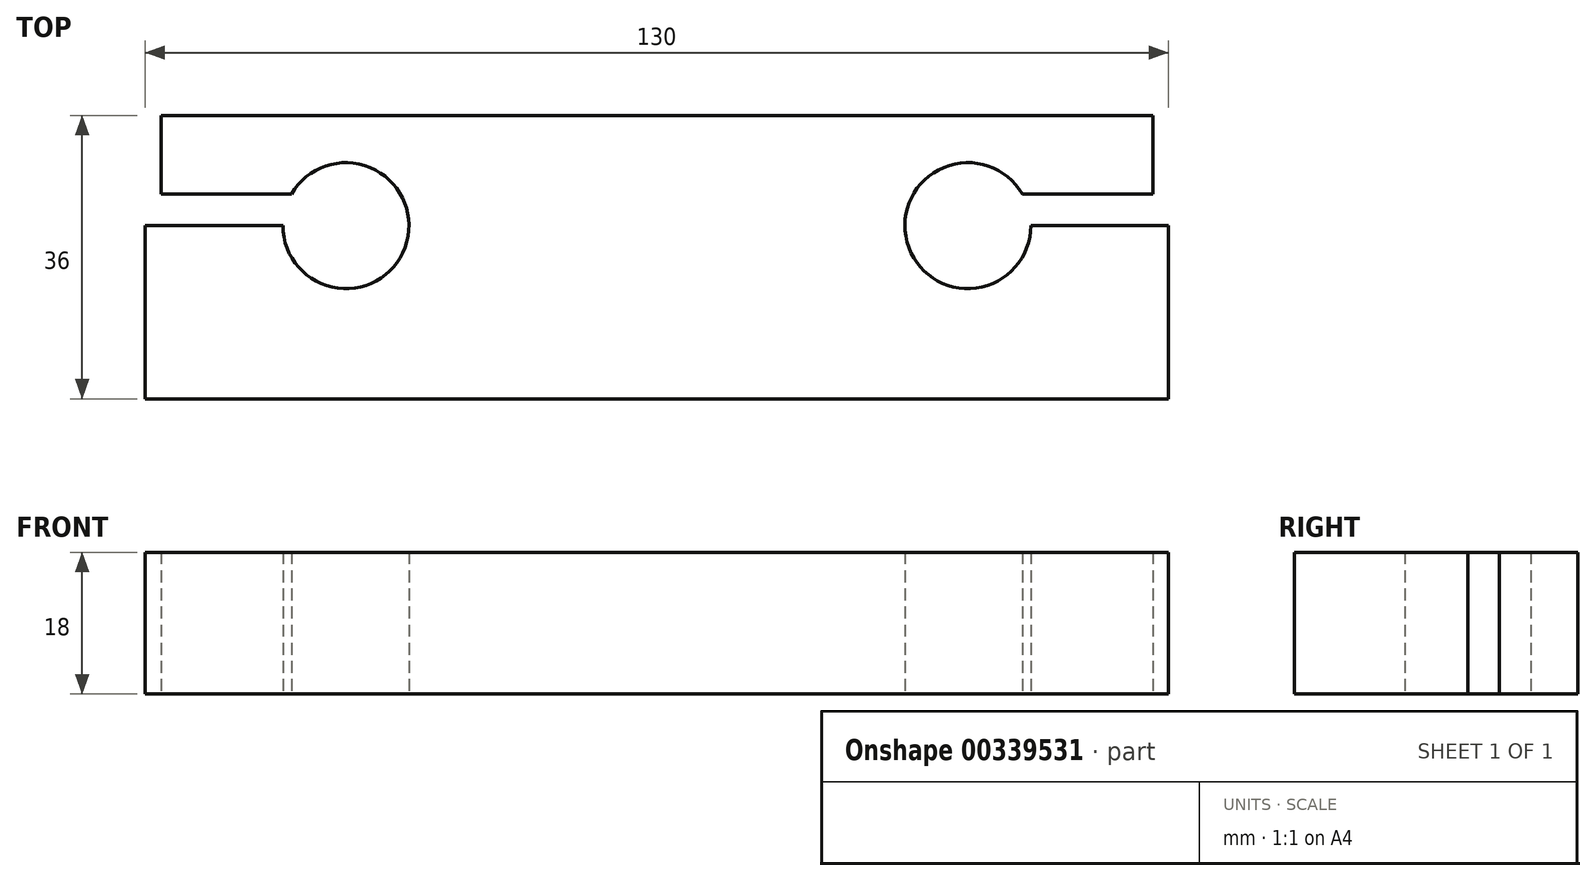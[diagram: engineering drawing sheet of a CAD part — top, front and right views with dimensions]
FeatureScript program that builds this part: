
annotation { "Feature Type Name" : "Feature", "Feature Type Description" : "" }
export const myFeature = defineFeature(function(context is Context, id is Id, definition is map)
    precondition{}
    {
        {
            var Q0;
            Q0=qCreatedBy(makeId("Top.planeOp"),FACE);
            var sketch = newSketch(context, id + "F0", { "sketchPlane" : qUnion([Q0])});
            skLineSegment(sketch, "E0.bottom", {"start": v(-86.35, 30.47) * mm, "end": v(43.65, 30.47) * mm});
            skLineSegment(sketch, "E0.top", {"start": v(-86.35, -5.53) * mm, "end": v(43.65, -5.53) * mm});
            skLineSegment(sketch, "E0.left", {"start": v(-86.35, 30.47) * mm, "end": v(-86.35, -5.53) * mm});
            skLineSegment(sketch, "E0.right", {"start": v(43.65, 30.47) * mm, "end": v(43.65, -5.53) * mm});
            skCircle(sketch, "E1", {"center": v(-60.85, 16.47) * mm, "radius": 8 * mm});
            skCircle(sketch, "E2", {"center": v(18.15, 16.47) * mm, "radius": 8 * mm});
            skCircle(sketch, "E3", {"center": v(-21.35, 16.47) * mm, "radius": 13 * mm});
            skPoint(sketch, "E3.centerSnap0", {"position": v(-21.35, -5.53) * mm});
            skLineSegment(sketch, "E4", {"start": v(-60.85, 16.47) * mm, "end": v(-86.35, 16.47) * mm});
            skLineSegment(sketch, "E5", {"start": v(18.15, 16.47) * mm, "end": v(43.65, 16.47) * mm});
            skLineSegment(sketch, "E6", {"start": v(43.65, 20.47) * mm, "end": v(16.67, 20.47) * mm});
            skLineSegment(sketch, "E7", {"start": v(-86.35, 20.47) * mm, "end": v(-60.85, 20.47) * mm});
            skSolve(sketch);
        }
        {
            var Q0;
            {var subQ9=sQuery(id+"F0.wireOp",EDGE,"E0.bottom");Q0=makeQuery(id+"F0.imprint","IMPRINT",FACE,{"disambiguationData":[TD([[makeQuery(id+"F0.imprint","IMPRINT",EDGE,{"derivedFrom":subQ9}),-1.0]])]});}
            var Q1;
            Q1=makeQuery(id+"F0.imprint","IMPRINT",FACE,{"disambiguationData":[TD([[makeQuery(id+"F0.imprint","IMPRINT",EDGE,{"derivedFrom":sQuery(id+"F0.wireOp",EDGE,"E3")}),1.0]])]});
            extrude(context, id + "F1", {"entities" : qUnion([Q0, Q1]), "depth" : 18 * mm});
        }
        {
            var Q0;
            {var subQ0=sQuery(id+"F0.wireOp",EDGE,"E0.left");Q0=makeQuery(id+"F1.opExtrude","SWEPT_FACE",FACE,{"disambiguationData":[OSD([subQ0]),TDD([makeQuery(id+"F0.imprint","IMPRINT",EDGE,{"disambiguationData":[TD([[makeQuery(id+"F0.imprint","INTERSECT",VERTEX,{"derivedFrom":[sQuery(id+"F0.wireOp",EDGE,"E0.bottom"),subQ0]}),-1.0]])],"derivedFrom":subQ0})])]});}
            extrude(context, id + "F2", {"entities" : qUnion([Q0]), "operationType" : NewBodyOperationType.REMOVE, "oppositeDirection" : true, "depth" : 2 * mm});
        }
        {
            var Q0;
            {var subQ0=sQuery(id+"F0.wireOp",EDGE,"E0.right");Q0=makeQuery(id+"F1.opExtrude","SWEPT_FACE",FACE,{"disambiguationData":[OSD([subQ0]),TDD([makeQuery(id+"F0.imprint","IMPRINT",EDGE,{"disambiguationData":[TD([[makeQuery(id+"F0.imprint","INTERSECT",VERTEX,{"derivedFrom":[sQuery(id+"F0.wireOp",EDGE,"E0.bottom"),subQ0]}),-1.0]])],"derivedFrom":subQ0})])]});}
            extrude(context, id + "F3", {"entities" : qUnion([Q0]), "operationType" : NewBodyOperationType.REMOVE, "oppositeDirection" : true, "depth" : 2 * mm});
        }
    });
